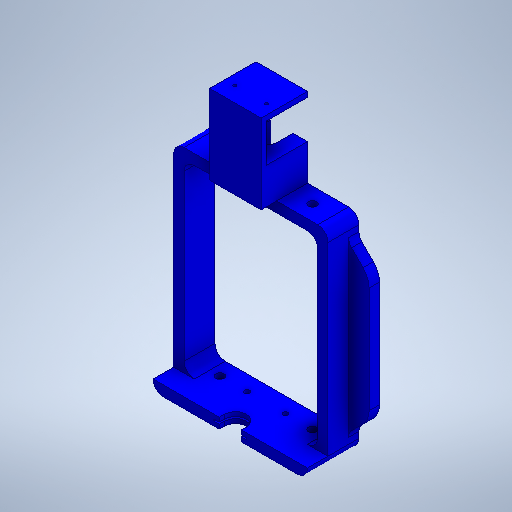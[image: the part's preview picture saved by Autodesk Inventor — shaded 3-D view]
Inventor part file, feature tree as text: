
AUTODESK INVENTOR PART (.ipt)
format: ipt  version: 2025.2 (Build 292293000, 293)  size: 451,072 bytes
history: native  units: mm
features: sketch x11, extrude x9, hole x5, fillet x4, other x1
ambient origin geometry x8: Origin, YZ Plane, XZ Plane, XY Plane, X Axis, Y Axis, Z Axis, Center Point
bodies: Solid1 (feature_tree)
feature tree (30):
  sketch  "Sketch1"  dims[d0=150.0mm d1=200.0mm]
  extrude  "Extrusion1"  Depth=200.0mm
  extrude  "Extrusion2"  Depth=10.0mm
  fillet  "Fillet1"  Radius=130.0mm
  sketch  "Sketch2"  dims[d2=10.0mm d3=10.0mm d4=130.0mm]
  hole  "Hole1"  [1 undecoded]
  hole  "Hole2"  [1 undecoded]
  hole  "Hole3"  [1 undecoded]
  hole  "Hole4"  [1 undecoded]
  sketch  "Sketch3"  dims[d5=180.0mm d6=40.0mm]
  other  "Work Axis1"
  sketch  "Sketch4"  dims[d7=20.0mm d8=40.0mm]
  extrude  "Extrusion3"  Depth=10.0mm
  sketch  "Sketch6"  dims[d11=40.0mm d12=30.0mm d13=0.0mm]
  extrude  "Extrusion4"  Depth=20.0mm
  extrude  "Extrusion5"  Depth=4.0mm
  hole  "Hole5"  [1 undecoded]
  fillet  "Fillet2"  Radius=15.0mm
  fillet  "Fillet3"  Radius=35.0mm
  extrude  "Extrusion6"  Depth=50.0mm
  extrude  "Extrusion7"  Depth=10.0mm
  extrude  "Extrusion8"  Depth=50.0mm
  extrude  "Extrusion9"  Depth=10.0mm
  fillet  "Fillet4"  Radius=43.5mm
  sketch  "Sketch5"  dims[d9=40.0mm d10=20.0mm]
  sketch  "Sketch7"  dims[d14=10.0mm d15=0.0mm d16=20.0mm]
  sketch  "Sketch8"  dims[d17=20.0mm d18=20.0mm]
  sketch  "Sketch9"  dims[d19=8.0mm d20=6.0mm d21=4.0mm d22=2.0mm d23=90.0deg d24=5.0mm d25=0.0mm]
  sketch  "Sketch10"  dims[d26=8.0mm d27=6.0mm d28=4.0mm d29=2.0mm d30=90.0deg d31=5.0mm d32=0.0mm d33=37.3mm]
  sketch  "Sketch11"  dims[d34=5.0mm d35=6.0mm d36=4.0mm d37=2.0mm d38=90.0deg d39=8.0mm d40=0.0mm d41=22.0mm d42=6.0mm d43=4.0mm d44=2.0mm d45=90.0deg d46=8.0mm d47=0.0mm d48=30.0mm d49=15.0mm d50=35.0mm d51=0.0mm d52=50.0mm d53=15.0mm d54=50.0mm d55=5.0mm d56=43.5mm d57=45.0deg d58=37.3mm d59=0.0mm d60=50.0mm d61=5.0mm d62=0.0mm d63=3.0mm d64=6.0mm d65=4.0mm d66=2.0mm d67=90.0deg d68=8.0mm d69=20.594885mm d70=10.0mm d71=10.0mm d72=0.05mm d73=50.0mm d74=0.0mm d75=20.0mm d76=0.0mm d77=21.4mm d79=5.0mm d80=0.0mm d81=0.0mm d82=1.8mm d83=32.0mm d84=25.0mm d85=0.0mm d86=10.0mm]
note: 5 required parameter values undecoded (feature->parameter linkage not recoverable at this tier; creation-order binding heuristic only, values carry confidence <= 0.55)
